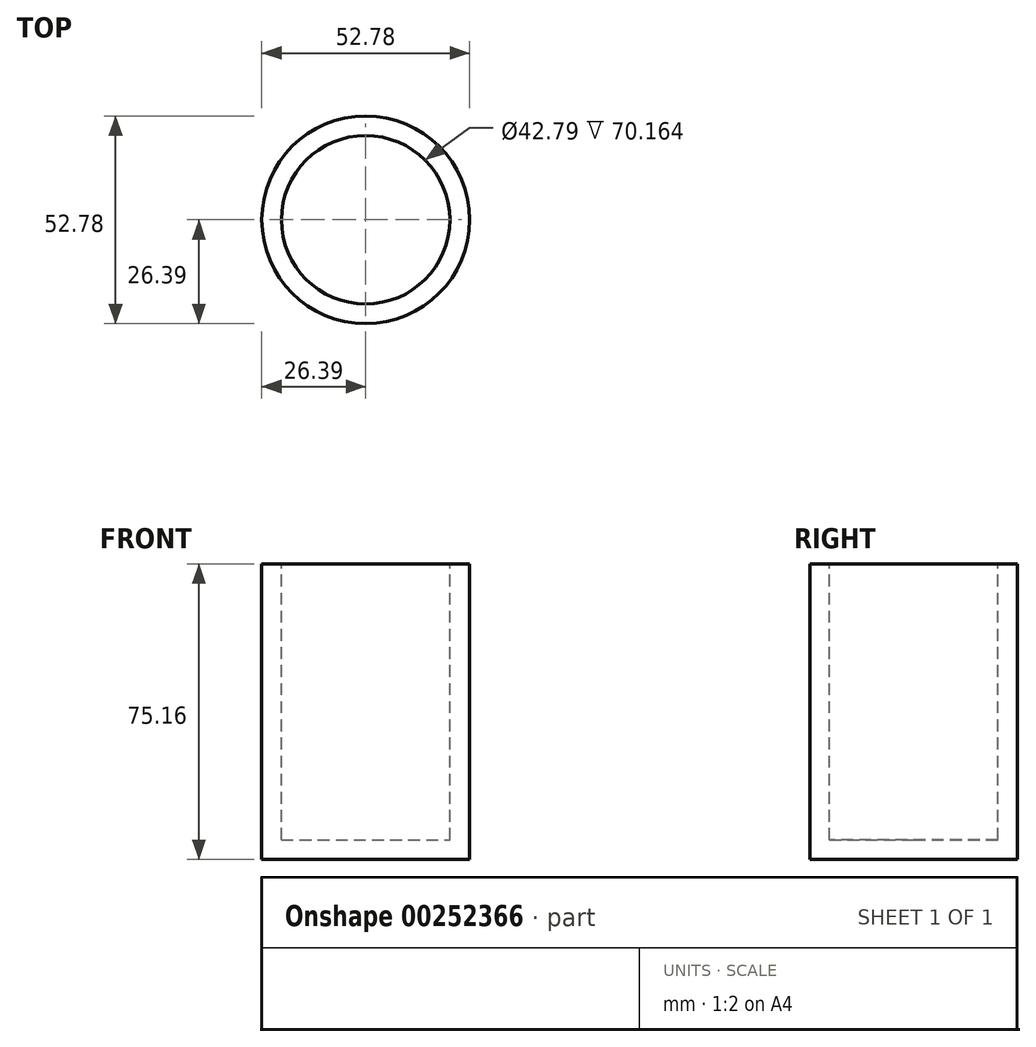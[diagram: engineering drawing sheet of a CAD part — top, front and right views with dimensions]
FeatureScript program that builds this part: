
annotation { "Feature Type Name" : "Feature", "Feature Type Description" : "" }
export const myFeature = defineFeature(function(context is Context, id is Id, definition is map)
    precondition{}
    {
        {
            var Q0;
            Q0=qCreatedBy(makeId("Front.planeOp"),FACE);
            var sketch = newSketch(context, id + "F0", { "sketchPlane" : qUnion([Q0])});
            skLineSegment(sketch, "E0.bottom", {"start": v(-26.4, 30.55) * mm, "end": v(28.69, 30.55) * mm});
            skLineSegment(sketch, "E0.top", {"start": v(-26.4, -44.61) * mm, "end": v(28.69, -44.61) * mm});
            skLineSegment(sketch, "E0.left", {"start": v(-26.4, 30.55) * mm, "end": v(-26.4, -44.61) * mm});
            skLineSegment(sketch, "E0.right", {"start": v(28.69, 30.55) * mm, "end": v(28.69, -44.61) * mm});
            skLineSegment(sketch, "E1", {"start": v(0, 30.55) * mm, "end": v(0, -44.61) * mm});
            skPoint(sketch, "E1.startSnap0", {"position": v(1.15, 30.55) * mm});
            skSolve(sketch);
        }
        {
            var Q0;
            {var subQ0=sQuery(id+"F0.wireOp",EDGE,"E0.left");Q0=makeQuery(id+"F0.imprint","IMPRINT",FACE,{"disambiguationData":[TD([[makeQuery(id+"F0.imprint","IMPRINT",EDGE,{"derivedFrom":subQ0}),1.0]])]});}
            var Q1;
            Q1=sQuery(id+"F0.wireOp",EDGE,"E1");
            revolve(context, id + "F1", {"entities" : qUnion([Q0]), "axis" : qUnion([Q1]), "revolveType" : RevolveType.FULL});
        }
        {
            var Q0;
            Q0=makeQuery(id+"F1.opRevolve","SWEPT_FACE",FACE,{"disambiguationData":[OSD([sQuery(id+"F0.wireOp",EDGE,"E0.bottom")])]});
            shell(context, id + "F2", {"entities" : qUnion([Q0]), "thickness" : 5 * mm});
        }
    });
